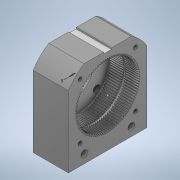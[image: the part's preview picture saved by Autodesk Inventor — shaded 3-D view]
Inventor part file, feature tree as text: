
AUTODESK INVENTOR PART (.ipt)
format: ipt  version: 2022 (Build 260153000, 153)  size: 1,541,120 bytes
history: mixed  units: mm
features: sketch x7, extrude x5, other x3, fillet x1, imported_body x1
ambient origin geometry x8: Origin, YZ Plane, XZ Plane, XY Plane, X Axis, Y Axis, Z Axis, Center Point
bodies: Solid1 (imported_parasolid)
feature tree (17):
  other  "Assembly2.iam"
  other  "96Gears_Stage_1_modified.ipt:1"
  other  "96Gears_Stage_2_modified.ipt:1"
  extrude  "Extrusion3"  Depth=3.0mm
  extrude  "Extrusion5"  Depth=1.0mm TaperAngle=0.0deg
  extrude  "Extrusion6"  Depth=6.0mm TaperAngle=0.0deg
  extrude  "Extrusion7"  TaperAngle=0.0deg  [1 undecoded]
  extrude  "Extrusion8"  Depth=3.5mm
  fillet  "Fillet1"  [1 undecoded]
  sketch  "Sketch11"  dims[d31=3.0mm d32=0.0mm d33=1.0mm d35=5.0mm]
  sketch  "Sketch5"  dims[d7=6.0mm d8=1.0mm d9=0.0mm]
  sketch  "Sketch4"  dims[d0=10.0mm d6=3.0mm]
  sketch  "Sketch7"  dims[d17=32.25mm d18=6.0mm d19=0.0mm]
  sketch  "Sketch8"  dims[d20=10.0mm d21=0.0mm d22=0.0mm]
  sketch  "Sketch9"  dims[d23=6.75mm d27=3.5mm d28=0.0mm d29=0.0mm]
  sketch  "Sketch10"  dims[d30=5.0mm]
  imported_body  NMx_Import_Brep_tag  [imported B-rep: ~819 faces, bbox_mm=[27.0, 66.5, 60.0]]
note: 2 required parameter values undecoded (feature->parameter linkage not recoverable at this tier; creation-order binding heuristic only, values carry confidence <= 0.55)
